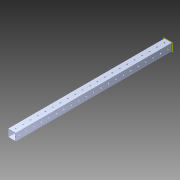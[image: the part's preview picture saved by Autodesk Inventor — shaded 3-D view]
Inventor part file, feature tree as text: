
AUTODESK INVENTOR PART (.ipt)
format: ipt  version: 2014 SP1 (Build 180222100, 222)  size: 1,236,992 bytes
history: native  units: in
note: dims shown in document units (in); Inventor stores cm internally (conversion verified against a paired STEP export)
features: pattern_circular x1, other x1, plane x1, extrude x1, imported_body x1, sketch x1
ambient origin geometry x8: Origin, YZ Plane, XZ Plane, XY Plane, X Axis, Y Axis, Z Axis, Center Point
bodies: Body1 (feature_tree)
feature tree (6):
  pattern_circular  "CirPattern2"
  other  "217-3426-STEP1"
  plane  "Work Plane1"
  extrude  "Extrusion1"  Depth=3937.0079in TaperAngle=0.0deg
  imported_body  "Base1"
  sketch  "Sketch1"  dims[d0=-21.0in d1=3937.0079in d2=0.0in]
